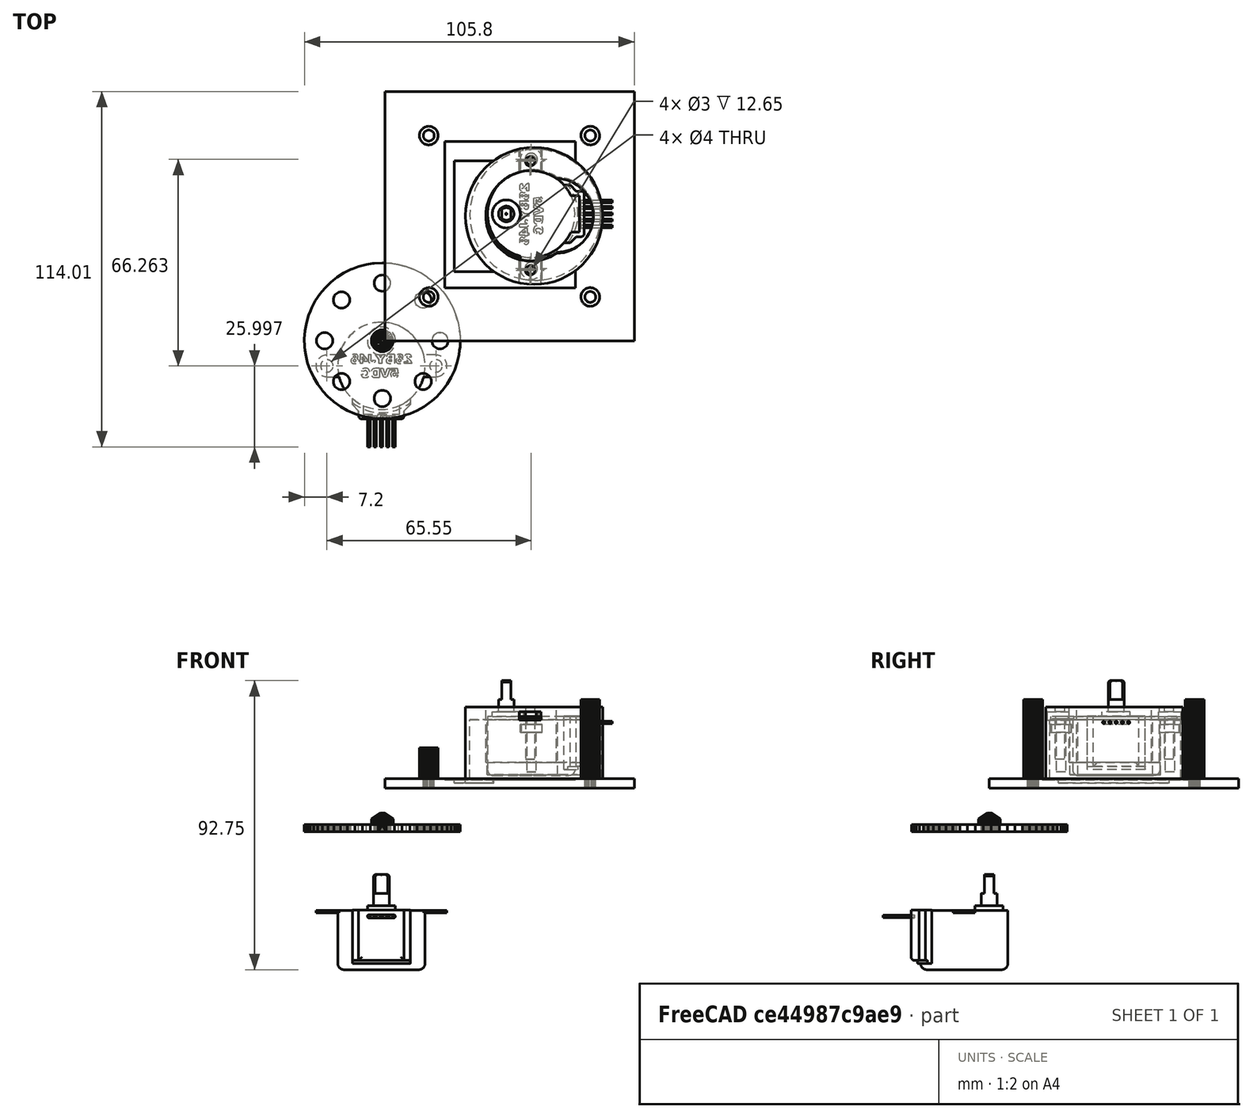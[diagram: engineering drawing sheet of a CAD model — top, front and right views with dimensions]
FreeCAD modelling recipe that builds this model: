
FCSTD DOCUMENT  (FreeCAD 0.20R29177 +426 (Git))
Label: food_hopper_assembly
License: All rights reserved
LicenseURL: http://en.wikipedia.org/wiki/All_rights_reserved
objects: Part::Cylinder×10, Part::Feature×8, Part::Box×6, Part::MultiFuse×4, Part::Cut×3, Part::Compound×1
note: 32 computed .brp shape members not serialized (recipe doc carries the construction recipe); baked Part::Feature solids carry a one-line shape summary decoded from their .brp

FEATURE [Part::Feature] Part__Feature  label="stepper_motor_model"
  Placement = pos=(0,0,0) rot=(-1,0,0;1.5708rad)
  shape: bbox 42 x 41.15 x 30.5 mm, 152 faces (baked)
FEATURE [Part::Feature] BOLTS_part  label="Hex socket countersunk head screw M3 20.0"
  Placement = pos=(17.1996,-8.01257,-15.25) rot=(1,0,0;3.14159rad)
  shape: bbox 6 x 6 x 20 mm, 12 faces (baked)
FEATURE [Part::Feature] BOLTS_part002  label="Hex socket countersunk head screw M3 20.001"
  Placement = pos=(-17.8004,-8.01257,-15.25) rot=(1,0,0;3.14159rad)
  shape: bbox 6 x 6 x 20 mm, 12 faces (baked)
FEATURE [Part::Feature] Part__Feature001  label="stepper_rendering"
  Placement = pos=(-0.300362,-8.01257,-24.25) rot=(-1,0,0;1.5708rad)
  shape: bbox 42 x 41.15 x 30.5 mm, 152 faces (baked)
FEATURE [Part::Box] Box  label="Cube"
  AttacherType = Attacher::AttachEngine3D
  Height = 2.6
  Length = 7
  Placement = pos=(13.8,-11.5126,-22.6) rot=(0,0,1;0rad)
  Width = 7
FEATURE [Part::Cylinder] Cylinder008
  Angle = 360
  AttacherType = Attacher::AttachEngine3D
  FirstAngle = 0
  Height = 20
  Placement = pos=(-0.300362,-16.31,-36.25) rot=(0,0,1;0rad)
  Radius = 12
  SecondAngle = 0
FEATURE [Part::Cylinder] Cylinder
  Angle = 360
  AttacherType = Attacher::AttachEngine3D
  FirstAngle = 0
  Height = 19
  Placement = pos=(-0.300362,-9.31302,-45) rot=(0,0,1;0rad)
  Radius = 21
  SecondAngle = 0
FEATURE [Part::Cylinder] Cylinder007
  Angle = 360
  AttacherType = Attacher::AttachEngine3D
  FirstAngle = 0
  Height = 20
  Placement = pos=(-0.300362,-8.31,-36.25) rot=(0,0,1;0rad)
  Radius = 14.5
  SecondAngle = 0
FEATURE [Part::Box] Box007  label="Cube007"
  AttacherType = Attacher::AttachEngine3D
  Height = 2.6
  Length = 7
  Placement = pos=(-21.3004,-11.5126,-22.6) rot=(0,0,1;0rad)
  Width = 7
FEATURE [Part::MultiFuse] Fusion003
  Placement = pos=(0,0,-7.5) rot=(0,0,1;0rad)
  Shapes = -> [Cylinder008,Cylinder007,Box,Box007,BOLTS_part,BOLTS_part002]
FEATURE [Part::Cut] Cut008  label="motor_fit"
  Base = -> Cylinder
  Placement = pos=(0,8,25) rot=(0,-1,0;0rad)
  Tool = -> Fusion003
FEATURE [Part::Compound] Compound
  Links = -> [Cut008,Part__Feature]
  Placement = pos=(47.75,40.75,38) rot=(0,0,1;1.5708rad)
FEATURE [Part::Feature] BOLTS_part003  label="Hex socket countersunk head screw M3 20.002"
  Placement = pos=(17.1996,-8.01257,-15.25) rot=(1,0,0;3.14159rad)
  shape: bbox 6 x 6 x 20 mm, 12 faces (baked)
FEATURE [Part::Feature] BOLTS_part004  label="Hex socket countersunk head screw M3 20.003"
  Placement = pos=(-17.8004,-8.01257,-15.25) rot=(1,0,0;3.14159rad)
  shape: bbox 6 x 6 x 20 mm, 12 faces (baked)
FEATURE [Part::Box] Box008  label="Cube008"
  AttacherType = Attacher::AttachEngine3D
  Height = 2.6
  Length = 8
  Placement = pos=(14,-11.5126,-22.6) rot=(0,0,1;0rad)
  Width = 7
FEATURE [Part::Cylinder] Cylinder010
  Angle = 360
  AttacherType = Attacher::AttachEngine3D
  FirstAngle = 0
  Height = 25
  Placement = pos=(-0.300362,-9.31302,-51) rot=(0,0,1;0rad)
  Radius = 22
  SecondAngle = 0
FEATURE [Part::Cylinder] Cylinder011
  Angle = 360
  AttacherType = Attacher::AttachEngine3D
  FirstAngle = 0
  Height = 20
  Placement = pos=(-0.300362,-16.31,-36.25) rot=(0,0,1;0rad)
  Radius = 12
  SecondAngle = 0
FEATURE [Part::Box] Box009  label="Cube009"
  AttacherType = Attacher::AttachEngine3D
  Height = 2.6
  Length = 8
  Placement = pos=(-22.7,-11.51,-22.6) rot=(0,0,1;0rad)
  Width = 7
FEATURE [Part::Cylinder] Cylinder012
  Angle = 360
  AttacherType = Attacher::AttachEngine3D
  FirstAngle = 0
  Height = 20
  Placement = pos=(-0.300362,-8.31,-36.25) rot=(0,0,1;0rad)
  Radius = 14.5
  SecondAngle = 0
FEATURE [Part::MultiFuse] Fusion004
  Placement = pos=(0,0,-7.5) rot=(0,0,1;0rad)
  Shapes = -> [Cylinder011,Cylinder012,Box008,Box009,BOLTS_part003,BOLTS_part004]
FEATURE [Part::Cut] Cut009  label="motor_fit001"
  Base = -> Cylinder010
  Placement = pos=(39.36,40.4,67) rot=(0,0,1;1.5708rad)
  Tool = -> Fusion004
FEATURE [Part::Box] Box010  label="Cube010"
  AttacherType = Attacher::AttachEngine3D
  Height = 15
  Length = 84
  Placement = pos=(-1,-1,0) rot=(0,0,1;0rad)
  Width = 84
FEATURE [Part::Box] Box011  label="Cube011"
  AttacherType = Attacher::AttachEngine3D
  Height = 46
  Length = 42
  Placement = pos=(20,17,17.6) rot=(0,0,1;0rad)
  Width = 47
FEATURE [Part::Cylinder] Cylinder013
  Angle = 360
  AttacherType = Attacher::AttachEngine3D
  FirstAngle = 0
  Height = 18
  Placement = pos=(14.0136,14.48,27.9) rot=(0,0,1;0rad)
  Radius = 5
  SecondAngle = 0
FEATURE [Part::Cylinder] Cylinder015
  Angle = 360
  AttacherType = Attacher::AttachEngine3D
  FirstAngle = 0
  Height = 16
  Placement = pos=(66.01,13.48,43.5) rot=(0,0,1;0rad)
  Radius = 5
  SecondAngle = 0
FEATURE [Part::Cylinder] Cylinder016
  Angle = 360
  AttacherType = Attacher::AttachEngine3D
  FirstAngle = 0
  Height = 18
  Placement = pos=(14.0136,66.4773,27.9) rot=(0,0,1;0rad)
  Radius = 5
  SecondAngle = 0
FEATURE [Part::Cylinder] Cylinder017
  Angle = 360
  AttacherType = Attacher::AttachEngine3D
  FirstAngle = 0
  Height = 16
  Placement = pos=(67.01,65.48,43.5) rot=(0,0,1;0rad)
  Radius = 5
  SecondAngle = 0
FEATURE [Part::Feature] Rotor_V10001_solid  label="larger_pellet_Rotor"
  Placement = pos=(-39.76,-40.7,-45) rot=(0,0,1;0rad)
  shape: bbox 49.98 x 50 x 6 mm, 2228 faces (baked)
FEATURE [Part::Feature] Motor_Base_V3001_solid  label="Motor_Base_V3001 (Solid)"
  shape: bbox 80 x 80 x 58.1 mm, 1286 faces (baked)
FEATURE [Part::MultiFuse] Fusion
  Shapes = -> [Cylinder017,Box010,Box011,Cylinder013,Cylinder015,Cylinder016]
FEATURE [Part::Cut] Cut
  Base = -> Motor_Base_V3001_solid
  Tool = -> Fusion
FEATURE [Part::MultiFuse] Fusion005  label="motor_base"
  Shapes = -> [Cut009,Cut]
